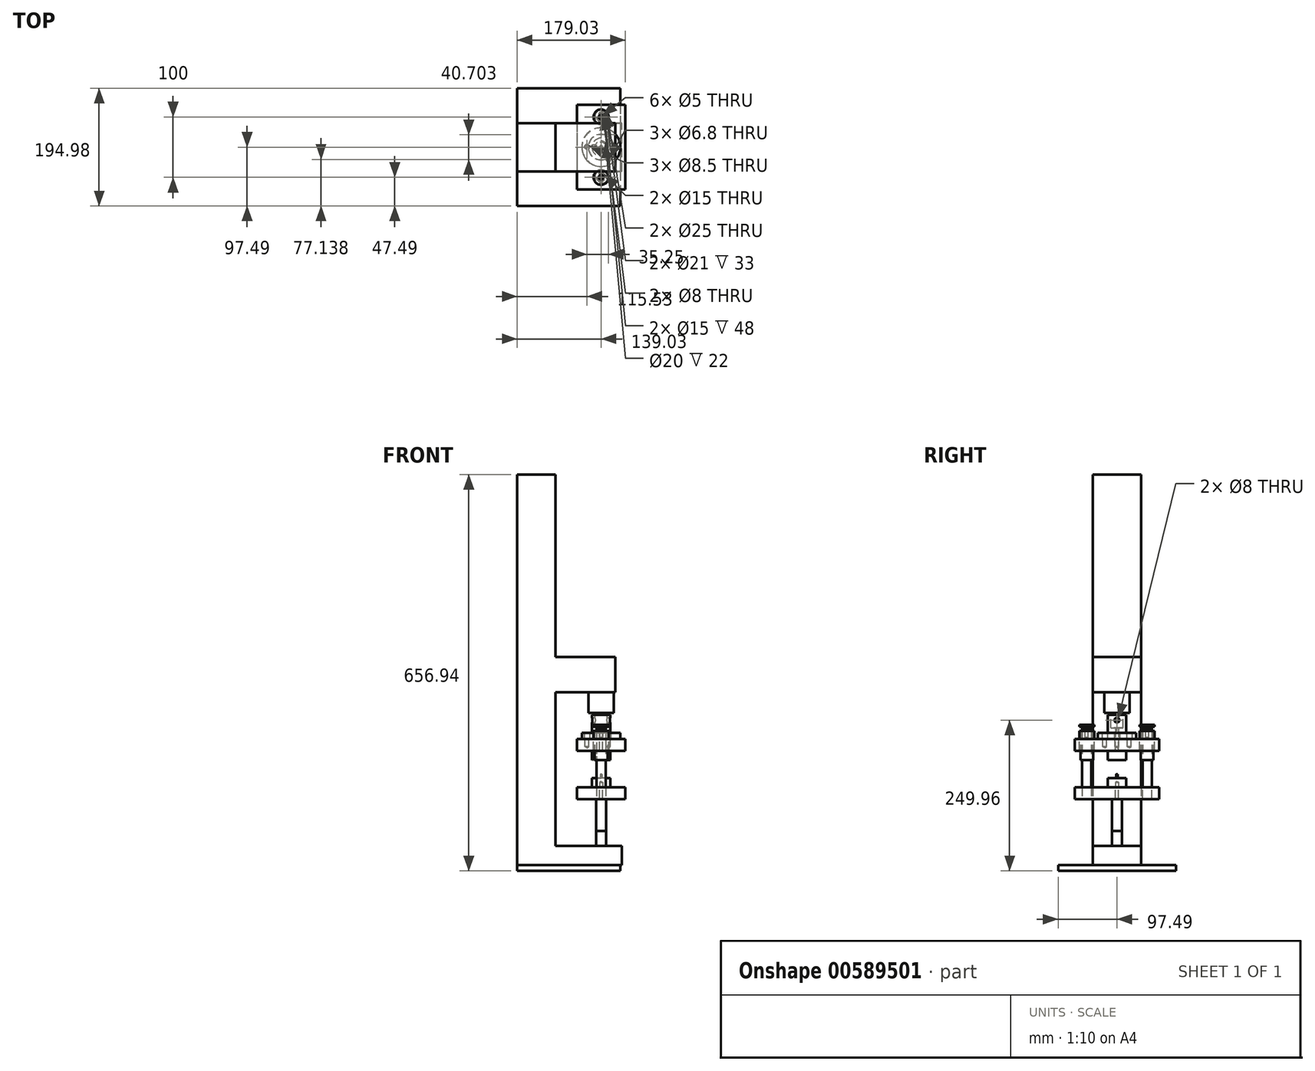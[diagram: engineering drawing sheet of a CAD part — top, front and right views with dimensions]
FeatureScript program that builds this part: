
annotation { "Feature Type Name" : "Feature", "Feature Type Description" : "" }
export const myFeature = defineFeature(function(context is Context, id is Id, definition is map)
    precondition{}
    {
        {
            assignVariable(context, id + "F0", {"name" : "Abstand", "anyValue" : 60});
        }
        {
            assignVariable(context, id + "F1", {"name" : "Hub", "anyValue" : 30});
        }
        {
            var Q0;
            Q0=qCreatedBy(makeId("Top.planeOp"),FACE);
            var sketch = newSketch(context, id + "F2", { "sketchPlane" : qUnion([Q0])});
            skLineSegment(sketch, "E0.bottom", {"start": v(40, 70) * mm, "end": v(-40, 70) * mm});
            skLineSegment(sketch, "E0.top", {"start": v(40, -70) * mm, "end": v(-40, -70) * mm});
            skLineSegment(sketch, "E0.left", {"start": v(40, 70) * mm, "end": v(40, -70) * mm});
            skLineSegment(sketch, "E0.right", {"start": v(-40, 70) * mm, "end": v(-40, -70) * mm});
            skPoint(sketch, "E0.middle", {"position": v(0, 0) * mm});
            skSolve(sketch);
        }
        {
            var Q0;
            Q0=makeQuery(id+"F2.imprint","IMPRINT",FACE,{"disambiguationData":[TD([[makeQuery(id+"F2.imprint","IMPRINT",EDGE,{"derivedFrom":sQuery(id+"F2.wireOp",EDGE,"E0.bottom")}),1.0]])]});
            extrude(context, id + "F3", {"entities" : qUnion([Q0]), "oppositeDirection" : true, "depth" : 20 * mm, "offsetDistance" : 25 * mm});
        }
        {
            var Q0;
            Q0=makeQuery(id+"F3.opExtrude","CAP_FACE",FACE,{"disambiguationData":[OSD([sQuery(id+"F2.wireOp",EDGE,"E0.bottom"),sQuery(id+"F2.wireOp",EDGE,"E0.top"),sQuery(id+"F2.wireOp",EDGE,"E0.left"),sQuery(id+"F2.wireOp",EDGE,"E0.right")])],"isStart":false});
            cPlane(context, id + "F4", {"entities" : qUnion([Q0]), "cplaneType" : CPlaneType.OFFSET, "offset" : (getVariable(context, 'Abstand')) * mm, "width" : 150 * mm, "height" : 150 * mm});
        }
        {
            var Q0;
            Q0=qCreatedBy(id+"F4.planeOp",FACE);
            var sketch = newSketch(context, id + "F5", { "sketchPlane" : qUnion([Q0])});
            skLineSegment(sketch, "E1.bottom", {"start": v(40, -70) * mm, "end": v(-40, -70) * mm});
            skLineSegment(sketch, "E1.top", {"start": v(40, 70) * mm, "end": v(-40, 70) * mm});
            skLineSegment(sketch, "E1.left", {"start": v(40, -70) * mm, "end": v(40, 70) * mm});
            skLineSegment(sketch, "E1.right", {"start": v(-40, -70) * mm, "end": v(-40, 70) * mm});
            skPoint(sketch, "E1.middle", {"position": v(0, 0) * mm});
            skSolve(sketch);
        }
        {
            var Q0;
            Q0 = qSketchRegion(id + "F5", true);
            extrude(context, id + "F6", {"entities" : qUnion([Q0]), "depth" : 20 * mm, "offsetDistance" : 25 * mm});
        }
        {
            var Q0;
            Q0=qCreatedBy(makeId("Top.planeOp"),FACE);
            var sketch = newSketch(context, id + "F7", { "sketchPlane" : qUnion([Q0])});
            skPoint(sketch, "E2", {"position": v(0, -50) * mm});
            skPoint(sketch, "E3", {"position": v(0, 50) * mm});
            skSolve(sketch);
        }
        {
            var Q0;
            Q0=sQuery(id+"F7.wireOp",VERTEX,"E2");
            var Q1;
            Q1=sQuery(id+"F7.wireOp",VERTEX,"E3");
            var Q2;
            Q2=makeQuery(id+"F3.opExtrude","SWEPT_BODY",BODY,{"disambiguationData":[OSD([sQuery(id+"F2.wireOp",EDGE,"E0.bottom"),sQuery(id+"F2.wireOp",EDGE,"E0.top"),sQuery(id+"F2.wireOp",EDGE,"E0.left"),sQuery(id+"F2.wireOp",EDGE,"E0.right")])]});
            hole(context, id + "F8", {"style" : HoleStyle.SIMPLE, "endStyle" : HoleEndStyle.THROUGH, "holeDiameter" : 25 * mm, "majorDiameter" : 3 * mm, "isTappedThrough" : true, "tappedDepth" : 11 * mm, "tapClearance" : 4, "startFromSketch" : true, "locations" : qUnion([Q0, Q1]), "scope" : qUnion([Q2])});
        }
        {
            var Q0;
            Q0=sQuery(id+"F7.wireOp",VERTEX,"E2");
            var Q1;
            Q1=sQuery(id+"F7.wireOp",VERTEX,"E3");
            var Q2;
            Q2=makeQuery(id+"F6.opExtrude","SWEPT_BODY",BODY,{"disambiguationData":[OSD([sQuery(id+"F5.wireOp",EDGE,"E1.bottom"),sQuery(id+"F5.wireOp",EDGE,"E1.top"),sQuery(id+"F5.wireOp",EDGE,"E1.left"),sQuery(id+"F5.wireOp",EDGE,"E1.right")])]});
            hole(context, id + "F9", {"style" : HoleStyle.SIMPLE, "endStyle" : HoleEndStyle.THROUGH, "holeDiameter" : 15 * mm, "majorDiameter" : 5 * mm, "isTappedThrough" : true, "tappedDepth" : 11 * mm, "tapClearance" : 4, "startFromSketch" : true, "locations" : qUnion([Q0, Q1]), "scope" : qUnion([Q2])});
        }
        {
            var Q0;
            Q0=qCreatedBy(makeId("Top.planeOp"),FACE);
            var sketch = newSketch(context, id + "F10", { "sketchPlane" : qUnion([Q0])});
            skCircle(sketch, "E4", {"center": v(0, -50) * mm, "radius": 7.5 * mm});
            skCircle(sketch, "E5", {"center": v(0, -50) * mm, "radius": 12.5 * mm});
            skCircle(sketch, "E6", {"center": v(0, -50) * mm, "radius": 10.5 * mm});
            skSolve(sketch);
        }
        {
            var Q0;
            Q0=makeQuery(id+"F10.imprint","IMPRINT",FACE,{"disambiguationData":[TD([[makeQuery(id+"F10.imprint","IMPRINT",EDGE,{"derivedFrom":sQuery(id+"F10.wireOp",EDGE,"E5")}),1.0]])]});
            extrude(context, id + "F11", {"entities" : qUnion([Q0]), "depth" : 13 * mm, "offsetDistance" : 25 * mm, "hasSecondDirection" : true, "secondDirectionOppositeDirection" : true, "secondDirectionDepth" : 20 * mm});
        }
        {
            var Q0;
            Q0=qCreatedBy(id+"F4.planeOp",FACE);
            var sketch = newSketch(context, id + "F12", { "sketchPlane" : qUnion([Q0])});
            skCircle(sketch, "E7", {"center": v(0, 50) * mm, "radius": 7.5 * mm});
            skSolve(sketch);
        }
        {
            var Q0;
            Q0 = qSketchRegion(id + "F12", true);
            var Q1;
            Q1=makeQuery(id+"F6.opExtrude","CAP_FACE",FACE,{"disambiguationData":[OSD([sQuery(id+"F5.wireOp",EDGE,"E1.bottom"),sQuery(id+"F5.wireOp",EDGE,"E1.top"),sQuery(id+"F5.wireOp",EDGE,"E1.left"),sQuery(id+"F5.wireOp",EDGE,"E1.right")])],"isStart":false});
            extrude(context, id + "F13", {"entities" : qUnion([Q0]), "oppositeDirection" : true, "depth" : 100 * mm, "offsetDistance" : 25 * mm, "hasSecondDirection" : true, "secondDirectionOppositeDirection" : false, "secondDirectionDepth" : 20 * mm, "secondDirectionBoundEntityFace" : qUnion([Q1])});
        }
        {
            var Q0;
            Q0=makeQuery(id+"F13.opExtrude","CAP_EDGE",EDGE,{"disambiguationData":[OSD([sQuery(id+"F12.wireOp",EDGE,"E7")])],"isStart":false});
            chamfer(context, id + "F14", {"entities" : qUnion([Q0]), "chamferType" : ChamferType.OFFSET_ANGLE, "width" : 3 * mm, "oppositeDirection" : false, "angle" : 15 * degree, "tangentPropagation" : true});
        }
        {
            var Q0;
            Q0=makeQuery(id+"F13.opExtrude","CAP_FACE",FACE,{"disambiguationData":[OSD([sQuery(id+"F12.wireOp",EDGE,"E7")])],"isStart":false});
            var sketch = newSketch(context, id + "F15", { "sketchPlane" : qUnion([Q0])});
            skPoint(sketch, "E8", {"position": v(0, -50) * mm});
            skSolve(sketch);
        }
        {
            var Q0;
            Q0=sQuery(id+"F15.wireOp",VERTEX,"E8");
            var Q1;
            Q1=makeQuery(id+"F13.opExtrude","SWEPT_BODY",BODY,{"disambiguationData":[OSD([sQuery(id+"F12.wireOp",EDGE,"E7")])]});
            hole(context, id + "F16", {"style" : HoleStyle.SIMPLE, "endStyle" : HoleEndStyle.BLIND, "standardTappedOrClearance" : lookupTablePath({ "standard" : "ISO", "engagement" : "75%", "pitch" : "1 mm", "size" : "M6", "type" : "Tapped" }), "standardBlindInLast" : lookupTablePath({ "standard" : "ISO", "engagement" : "75%", "pitch" : "1 mm", "size" : "M6", "type" : "Tapped" }), "holeDiameter" : 5 * mm, "majorDiameter" : 6 * mm, "showTappedDepth" : true, "holeDepth" : 18 * mm, "isTappedThrough" : true, "tappedDepth" : 15 * mm, "tapClearance" : 3, "startFromSketch" : true, "locations" : qUnion([Q0]), "scope" : qUnion([Q1])});
        }
        {
            var Q0;
            Q0=makeQuery(id+"F13.opExtrude","CAP_FACE",FACE,{"disambiguationData":[OSD([sQuery(id+"F12.wireOp",EDGE,"E7")])],"isStart":false});
            var sketch = newSketch(context, id + "F17", { "sketchPlane" : qUnion([Q0])});
            skCircle(sketch, "E9", {"center": v(0, -50) * mm, "radius": 12.5 * mm});
            skCircle(sketch, "E10", {"center": v(0, -50) * mm, "radius": 4 * mm});
            skSolve(sketch);
        }
        {
            var Q0;
            Q0 = qSketchRegion(id + "F17", true);
            extrude(context, id + "F18", {"entities" : qUnion([Q0]), "depth" : 3 * mm, "offsetDistance" : 25 * mm});
        }
        {
            var Q0;
            Q0=makeQuery(id+"F3.opExtrude","CAP_FACE",FACE,{"disambiguationData":[OSD([sQuery(id+"F2.wireOp",EDGE,"E0.bottom"),sQuery(id+"F2.wireOp",EDGE,"E0.top"),sQuery(id+"F2.wireOp",EDGE,"E0.left"),sQuery(id+"F2.wireOp",EDGE,"E0.right")])],"isStart":false});
            cPlane(context, id + "F19", {"entities" : qUnion([Q0]), "cplaneType" : CPlaneType.OFFSET, "offset" : ((getVariable(context, 'Abstand') - getVariable(context, 'Hub')) / 2) * mm, "width" : 150 * mm, "height" : 150 * mm});
        }
        {
            var Q0;
            Q0=qCreatedBy(id+"F19.planeOp",FACE);
            var sketch = newSketch(context, id + "F20", { "sketchPlane" : qUnion([Q0])});
            skCircle(sketch, "E11", {"center": v(0, 50) * mm, "radius": 10.5 * mm});
            skCircle(sketch, "E12", {"center": v(0, 50) * mm, "radius": 7.5 * mm});
            skSolve(sketch);
        }
        {
            var Q0;
            Q0=makeQuery(id+"F20.imprint","IMPRINT",FACE,{"disambiguationData":[TD([[makeQuery(id+"F20.imprint","IMPRINT",EDGE,{"derivedFrom":sQuery(id+"F20.wireOp",EDGE,"E11")}),1.0]])]});
            extrude(context, id + "F21", {"entities" : qUnion([Q0]), "oppositeDirection" : true, "depth" : 48 * mm, "offsetDistance" : 25 * mm});
        }
        {
            var Q0;
            Q0=makeQuery(id+"F21.opExtrude","SWEPT_BODY",BODY,{"disambiguationData":[OSD([sQuery(id+"F20.wireOp",EDGE,"E11"),sQuery(id+"F20.wireOp",EDGE,"E12")])]});
            var Q1;
            Q1=makeQuery(id+"F11.opExtrude","SWEPT_BODY",BODY,{"disambiguationData":[OSD([sQuery(id+"F10.wireOp",EDGE,"E5"),sQuery(id+"F10.wireOp",EDGE,"E6")])]});
            var Q2;
            Q2=makeQuery(id+"F13.opExtrude","SWEPT_BODY",BODY,{"disambiguationData":[OSD([sQuery(id+"F12.wireOp",EDGE,"E7")])]});
            var Q3;
            Q3=makeQuery(id+"F18.opExtrude","SWEPT_BODY",BODY,{"disambiguationData":[OSD([sQuery(id+"F17.wireOp",EDGE,"E9"),sQuery(id+"F17.wireOp",EDGE,"E10")])]});
            var Q4;
            Q4=qCreatedBy(makeId("Front.planeOp"),FACE);
            mirror(context, id + "F22", {"entities" : qUnion([Q0, Q1, Q2, Q3]), "mirrorPlane" : qUnion([Q4])});
        }
        {
            var Q0;
            Q0=qCreatedBy(makeId("Right.planeOp"),FACE);
            var sketch = newSketch(context, id + "F23", { "sketchPlane" : qUnion([Q0])});
            skLineSegment(sketch, "E13", {"start": v(0, 0) * mm, "end": v(0, 71.02) * mm, "construction": true});
            skLineSegment(sketch, "E14", {"start": v(0, 0) * mm, "end": v(32, 0) * mm});
            skLineSegment(sketch, "E15", {"start": v(32, 0) * mm, "end": v(32, 10) * mm});
            skLineSegment(sketch, "E16", {"start": v(15, 10) * mm, "end": v(15, 40) * mm});
            skLineSegment(sketch, "E17", {"start": v(15, 40) * mm, "end": v(0, 40) * mm});
            skLineSegment(sketch, "E18", {"start": v(15, 10) * mm, "end": v(32, 10) * mm});
            skLineSegment(sketch, "E19", {"start": v(0, 40) * mm, "end": v(0, 0) * mm});
            skSolve(sketch);
        }
        {
            var Q0;
            Q0 = qSketchRegion(id + "F23", true);
            var Q1;
            Q1=sQuery(id+"F23.wireOp",EDGE,"E13");
            revolve(context, id + "F24", {"entities" : qUnion([Q0]), "axis" : qUnion([Q1]), "revolveType" : RevolveType.FULL});
        }
        {
            var Q0;
            Q0=makeQuery(id+"F24.opRevolve","SWEPT_FACE",FACE,{"disambiguationData":[OSD([sQuery(id+"F23.wireOp",EDGE,"E17")])]});
            var sketch = newSketch(context, id + "F25", { "sketchPlane" : qUnion([Q0])});
            skCircle(sketch, "E20", {"center": v(0, 0) * mm, "radius": 10 * mm});
            skSolve(sketch);
        }
        {
            var Q0;
            Q0 = qSketchRegion(id + "F25", true);
            extrude(context, id + "F26", {"entities" : qUnion([Q0]), "operationType" : NewBodyOperationType.REMOVE, "oppositeDirection" : true, "depth" : 22 * mm, "offsetDistance" : 25 * mm});
        }
        {
            var Q0;
            Q0=qCreatedBy(makeId("Right.planeOp"),FACE);
            var sketch = newSketch(context, id + "F27", { "sketchPlane" : qUnion([Q0])});
            skCircle(sketch, "E21", {"center": v(0, 31) * mm, "radius": 4 * mm});
            skSolve(sketch);
        }
        {
            var Q0;
            Q0 = qSketchRegion(id + "F27", true);
            extrude(context, id + "F28", {"entities" : qUnion([Q0]), "operationType" : NewBodyOperationType.REMOVE, "endBound" : BoundingType.THROUGH_ALL, "oppositeDirection" : true, "depth" : 25 * mm, "offsetDistance" : 25 * mm, "hasSecondDirection" : true, "secondDirectionBound" : SecondDirectionBoundingType.THROUGH_ALL, "secondDirectionOppositeDirection" : false, "secondDirectionDepth" : 25 * mm});
        }
        {
            var Q0;
            Q0=qCreatedBy(makeId("Top.planeOp"),FACE);
            var sketch = newSketch(context, id + "F29", { "sketchPlane" : qUnion([Q0])});
            skCircle(sketch, "E22", {"center": v(0, 0) * mm, "radius": 23.5 * mm, "construction": true});
            skPoint(sketch, "E23", {"position": v(11.75, -20.35) * mm});
            skPoint(sketch, "E24", {"position": v(-23.5, 0) * mm});
            skPoint(sketch, "E25", {"position": v(11.75, 20.35) * mm});
            skLineSegment(sketch, "E26", {"start": v(0, 0) * mm, "end": v(11.75, -20.35) * mm});
            skLineSegment(sketch, "E27", {"start": v(0, 0) * mm, "end": v(-23.5, 0) * mm});
            skLineSegment(sketch, "E28", {"start": v(0, 0) * mm, "end": v(11.75, 20.35) * mm});
            skCircle(sketch, "E29", {"center": v(-23.5, 0) * mm, "radius": 6.5 * mm, "construction": true});
            skSolve(sketch);
        }
        {
            var Q0;
            Q0=sQuery(id+"F29.wireOp",VERTEX,"E25");
            var Q1;
            Q1=sQuery(id+"F29.wireOp",VERTEX,"E24");
            var Q2;
            Q2=sQuery(id+"F29.wireOp",VERTEX,"E23");
            var Q3;
            Q3=makeQuery(id+"F24.opRevolve","SWEPT_BODY",BODY,{"disambiguationData":[OSD([sQuery(id+"F23.wireOp",EDGE,"E14"),sQuery(id+"F23.wireOp",EDGE,"E15"),sQuery(id+"F23.wireOp",EDGE,"E16"),sQuery(id+"F23.wireOp",EDGE,"E17"),sQuery(id+"F23.wireOp",EDGE,"E18"),sQuery(id+"F23.wireOp",EDGE,"E19")])]});
            hole(context, id + "F30", {"style" : HoleStyle.SIMPLE, "endStyle" : HoleEndStyle.THROUGH, "oppositeDirection" : true, "holeDiameter" : 8.5 * mm, "majorDiameter" : 5 * mm, "isTappedThrough" : true, "tappedDepth" : 11 * mm, "tapClearance" : 4, "startFromSketch" : true, "locations" : qUnion([Q0, Q1, Q2]), "scope" : qUnion([Q3])});
        }
        {
            var Q0;
            Q0=sQuery(id+"F29.wireOp",VERTEX,"E22.center");
            var Q1;
            Q1=makeQuery(id+"F24.opRevolve","SWEPT_BODY",BODY,{"disambiguationData":[OSD([sQuery(id+"F23.wireOp",EDGE,"E14"),sQuery(id+"F23.wireOp",EDGE,"E15"),sQuery(id+"F23.wireOp",EDGE,"E16"),sQuery(id+"F23.wireOp",EDGE,"E17"),sQuery(id+"F23.wireOp",EDGE,"E18"),sQuery(id+"F23.wireOp",EDGE,"E19")])]});
            hole(context, id + "F31", {"style" : HoleStyle.SIMPLE, "endStyle" : HoleEndStyle.THROUGH, "oppositeDirection" : true, "holeDiameter" : 5 * mm, "majorDiameter" : 5 * mm, "isTappedThrough" : true, "tappedDepth" : 8 * mm, "tapClearance" : 4, "startFromSketch" : true, "locations" : qUnion([Q0]), "scope" : qUnion([Q1])});
        }
        {
            var Q0;
            Q0=qCreatedBy(id+"F4.planeOp",FACE);
            var sketch = newSketch(context, id + "F32", { "sketchPlane" : qUnion([Q0])});
            skCircle(sketch, "E30", {"center": v(0, 0) * mm, "radius": 15 * mm});
            skSolve(sketch);
        }
        {
            var Q0;
            Q0 = qSketchRegion(id + "F32", true);
            extrude(context, id + "F33", {"entities" : qUnion([Q0]), "oppositeDirection" : true, "depth" : 15 * mm, "offsetDistance" : 25 * mm});
        }
        {
            var Q0;
            Q0=makeQuery(id+"F33.opExtrude","CAP_FACE",FACE,{"disambiguationData":[OSD([sQuery(id+"F32.wireOp",EDGE,"E30")])],"isStart":true});
            var sketch = newSketch(context, id + "F34", { "sketchPlane" : qUnion([Q0])});
            skPoint(sketch, "E31", {"position": v(0, 0) * mm});
            skSolve(sketch);
        }
        {
            var Q0;
            Q0=sQuery(id+"F34.wireOp",VERTEX,"E31");
            var Q1;
            Q1=makeQuery(id+"F33.opExtrude","SWEPT_BODY",BODY,{"disambiguationData":[OSD([sQuery(id+"F32.wireOp",EDGE,"E30")])]});
            hole(context, id + "F35", {"style" : HoleStyle.SIMPLE, "endStyle" : HoleEndStyle.BLIND, "holeDiameter" : 5 * mm, "majorDiameter" : 6 * mm, "holeDepth" : 8 * mm, "isTappedThrough" : true, "tappedDepth" : 16 * mm, "tapClearance" : 3, "startFromSketch" : true, "locations" : qUnion([Q0]), "scope" : qUnion([Q1])});
        }
        {
            var Q0;
            Q0=makeQuery(id+"F3.opExtrude","CAP_FACE",FACE,{"disambiguationData":[OSD([sQuery(id+"F2.wireOp",EDGE,"E0.bottom"),sQuery(id+"F2.wireOp",EDGE,"E0.top"),sQuery(id+"F2.wireOp",EDGE,"E0.left"),sQuery(id+"F2.wireOp",EDGE,"E0.right")])],"isStart":false});
            var sketch = newSketch(context, id + "F36", { "sketchPlane" : qUnion([Q0])});
            skCircle(sketch, "E32", {"center": v(0, 0) * mm, "radius": 15 * mm});
            skSolve(sketch);
        }
        {
            var Q0;
            Q0=makeQuery(id+"F36.imprint","IMPRINT",FACE,{"disambiguationData":[TD([[makeQuery(id+"F36.imprint","IMPRINT",EDGE,{"derivedFrom":sQuery(id+"F36.wireOp",EDGE,"E32")}),1.0]])]});
            extrude(context, id + "F37", {"entities" : qUnion([Q0]), "depth" : 15 * mm, "offsetDistance" : 25 * mm});
        }
        {
            var Q0;
            Q0=sQuery(id+"F29.wireOp",VERTEX,"E25");
            var Q1;
            Q1=sQuery(id+"F29.wireOp",VERTEX,"E24");
            var Q2;
            Q2=sQuery(id+"F29.wireOp",VERTEX,"E23");
            var Q3;
            Q3=makeQuery(id+"F3.opExtrude","SWEPT_BODY",BODY,{"disambiguationData":[OSD([sQuery(id+"F2.wireOp",EDGE,"E0.bottom"),sQuery(id+"F2.wireOp",EDGE,"E0.top"),sQuery(id+"F2.wireOp",EDGE,"E0.left"),sQuery(id+"F2.wireOp",EDGE,"E0.right")])]});
            hole(context, id + "F38", {"style" : HoleStyle.SIMPLE, "endStyle" : HoleEndStyle.BLIND, "standardTappedOrClearance" : lookupTablePath({ "standard" : "ISO", "engagement" : "75%", "pitch" : "1.25 mm", "size" : "M8", "type" : "Tapped" }), "standardBlindInLast" : lookupTablePath({ "standard" : "ISO", "engagement" : "75%", "pitch" : "1.25 mm", "size" : "M8", "type" : "Tapped" }), "holeDiameter" : 6.8 * mm, "majorDiameter" : 8 * mm, "showTappedDepth" : true, "holeDepth" : 13 * mm, "isTappedThrough" : true, "tappedDepth" : 8 * mm, "tapClearance" : 4, "startFromSketch" : true, "locations" : qUnion([Q0, Q1, Q2]), "scope" : qUnion([Q3])});
        }
        {
            var Q0;
            Q0=sQuery(id+"F29.wireOp",VERTEX,"E26.start");
            var Q1;
            Q1=makeQuery(id+"F3.opExtrude","SWEPT_BODY",BODY,{"disambiguationData":[OSD([sQuery(id+"F2.wireOp",EDGE,"E0.bottom"),sQuery(id+"F2.wireOp",EDGE,"E0.top"),sQuery(id+"F2.wireOp",EDGE,"E0.left"),sQuery(id+"F2.wireOp",EDGE,"E0.right")])]});
            var Q2;
            Q2=makeQuery(id+"F6.opExtrude","SWEPT_BODY",BODY,{"disambiguationData":[OSD([sQuery(id+"F5.wireOp",EDGE,"E1.bottom"),sQuery(id+"F5.wireOp",EDGE,"E1.top"),sQuery(id+"F5.wireOp",EDGE,"E1.left"),sQuery(id+"F5.wireOp",EDGE,"E1.right")])]});
            hole(context, id + "F39", {"style" : HoleStyle.SIMPLE, "endStyle" : HoleEndStyle.THROUGH, "holeDiameter" : 5 * mm, "majorDiameter" : 8 * mm, "isTappedThrough" : true, "tappedDepth" : 8 * mm, "tapClearance" : 4, "startFromSketch" : true, "locations" : qUnion([Q0]), "scope" : qUnion([Q1, Q2])});
        }
        {
            var Q0;
            Q0=makeQuery(id+"F33.opExtrude","CAP_FACE",FACE,{"disambiguationData":[OSD([sQuery(id+"F32.wireOp",EDGE,"E30")])],"isStart":false});
            var sketch = newSketch(context, id + "F40", { "sketchPlane" : qUnion([Q0])});
            skCircle(sketch, "E33", {"center": v(0, 0) * mm, "radius": 1.5 * mm});
            skSolve(sketch);
        }
        {
            var Q0;
            Q0=makeQuery(id+"F40.imprint","IMPRINT",FACE,{"disambiguationData":[TD([[makeQuery(id+"F40.imprint","IMPRINT",EDGE,{"derivedFrom":sQuery(id+"F40.wireOp",EDGE,"E33")}),1.0]])]});
            extrude(context, id + "F41", {"entities" : qUnion([Q0]), "depth" : 6 * mm, "offsetDistance" : 25 * mm});
        }
        {
            var Q0;
            Q0=qCreatedBy(makeId("Front.planeOp"),FACE);
            var sketch = newSketch(context, id + "F42", { "sketchPlane" : qUnion([Q0])});
            skLineSegment(sketch, "E34", {"start": v(-75.22, 77) * mm, "end": v(-75.22, -177.54) * mm});
            skLineSegment(sketch, "E35", {"start": v(-75.22, -177.54) * mm, "end": v(34.17, -177.54) * mm});
            skLineSegment(sketch, "E36", {"start": v(34.17, -177.54) * mm, "end": v(34.17, -208.96) * mm});
            skLineSegment(sketch, "E37", {"start": v(34.17, -208.96) * mm, "end": v(-139.03, -208.96) * mm});
            skLineSegment(sketch, "E38", {"start": v(-139.03, -208.96) * mm, "end": v(-139.03, 437.98) * mm});
            skLineSegment(sketch, "E39", {"start": v(-139.03, 437.98) * mm, "end": v(-75.22, 437.98) * mm});
            skLineSegment(sketch, "E40", {"start": v(-75.22, 437.98) * mm, "end": v(-75.22, 135.74) * mm});
            skLineSegment(sketch, "E41", {"start": v(-75.22, 77) * mm, "end": v(23.42, 77) * mm});
            skLineSegment(sketch, "E42", {"start": v(23.42, 77) * mm, "end": v(23.42, 135.74) * mm});
            skLineSegment(sketch, "E43", {"start": v(23.42, 135.74) * mm, "end": v(-75.22, 135.74) * mm});
            skSolve(sketch);
        }
        {
            var Q0;
            Q0=makeQuery(id+"F42.imprint","IMPRINT",FACE,{"disambiguationData":[TD([[makeQuery(id+"F42.imprint","IMPRINT",EDGE,{"derivedFrom":sQuery(id+"F42.wireOp",EDGE,"E34")}),-1.0]])]});
            extrude(context, id + "F43", {"entities" : qUnion([Q0]), "depth" : 40 * mm, "offsetDistance" : 25 * mm, "hasSecondDirection" : true, "secondDirectionOppositeDirection" : true, "secondDirectionDepth" : 40 * mm});
        }
        {
            var Q0;
            Q0=makeQuery(id+"F43.opExtrude","SWEPT_FACE",FACE,{"disambiguationData":[OSD([sQuery(id+"F42.wireOp",EDGE,"E41")])]});
            var sketch = newSketch(context, id + "F44", { "sketchPlane" : qUnion([Q0])});
            skCircle(sketch, "E44", {"center": v(0, 0) * mm, "radius": 21.2 * mm});
            skSolve(sketch);
        }
        {
            var Q0;
            Q0=makeQuery(id+"F44.imprint","IMPRINT",FACE,{"disambiguationData":[TD([[makeQuery(id+"F44.imprint","IMPRINT",EDGE,{"derivedFrom":sQuery(id+"F44.wireOp",EDGE,"E44")}),1.0]])]});
            extrude(context, id + "F45", {"entities" : qUnion([Q0]), "operationType" : NewBodyOperationType.ADD, "depth" : 34 * mm, "offsetDistance" : 25 * mm});
        }
        {
            var Q0;
            Q0=makeQuery(id+"F43.opExtrude","SWEPT_FACE",FACE,{"disambiguationData":[OSD([sQuery(id+"F42.wireOp",EDGE,"E35")])]});
            var sketch = newSketch(context, id + "F46", { "sketchPlane" : qUnion([Q0])});
            skCircle(sketch, "E45", {"center": v(0, 0) * mm, "radius": 8.37 * mm});
            skSolve(sketch);
        }
        {
            var Q0;
            Q0=makeQuery(id+"F46.imprint","IMPRINT",FACE,{"disambiguationData":[TD([[makeQuery(id+"F46.imprint","IMPRINT",EDGE,{"derivedFrom":sQuery(id+"F46.wireOp",EDGE,"E45")}),1.0]])]});
            extrude(context, id + "F47", {"entities" : qUnion([Q0]), "operationType" : NewBodyOperationType.ADD, "depth" : 25 * mm, "offsetDistance" : 25 * mm});
        }
        {
            var Q0;
            Q0=makeQuery(id+"F43.opExtrude","SWEPT_FACE",FACE,{"disambiguationData":[OSD([sQuery(id+"F42.wireOp",EDGE,"E37")])]});
            var sketch = newSketch(context, id + "F48", { "sketchPlane" : qUnion([Q0])});
            skLineSegment(sketch, "E46.bottom", {"start": v(-139.03, -97.5) * mm, "end": v(31.78, -97.5) * mm});
            skLineSegment(sketch, "E46.top", {"start": v(-139.03, 97.5) * mm, "end": v(31.78, 97.5) * mm});
            skLineSegment(sketch, "E46.left", {"start": v(-139.03, -97.5) * mm, "end": v(-139.03, 97.5) * mm});
            skLineSegment(sketch, "E46.right", {"start": v(31.78, -97.5) * mm, "end": v(31.78, 97.5) * mm});
            skPoint(sketch, "E46.middle", {"position": v(-53.62, 0) * mm});
            skSolve(sketch);
        }
        {
            var Q0;
            Q0 = qSketchRegion(id + "F48", true);
            extrude(context, id + "F49", {"entities" : qUnion([Q0]), "operationType" : NewBodyOperationType.ADD, "depth" : 10 * mm, "offsetDistance" : 25 * mm});
        }
        {
            var Q0;
            Q0=makeQuery(id+"F47.opExtrude","CAP_FACE",FACE,{"disambiguationData":[OSD([sQuery(id+"F46.wireOp",EDGE,"E45")])],"isStart":false});
            extrude(context, id + "F50", {"entities" : qUnion([Q0]), "depth" : 52.8 * mm, "offsetDistance" : 25 * mm});
        }
    });
